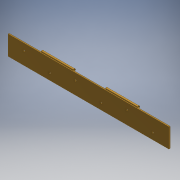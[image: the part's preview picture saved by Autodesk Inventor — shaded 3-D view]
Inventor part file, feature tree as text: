
AUTODESK INVENTOR PART (.ipt)
format: ipt  version: 2018 (Build 220112000, 112)  size: 174,080 bytes
history: native  units: mm
features: extrude x5, sketch x5, hole x1
ambient origin geometry x8: Origin, YZ Plane, XZ Plane, XY Plane, X Axis, Y Axis, Z Axis, Center Point
bodies: Solid1 (feature_tree)
feature tree (11):
  extrude  "Extrusion1"  Depth=30.0mm
  sketch  "Sketch2"  dims[d2=2.0mm d3=0.0mm d4=2.5mm]
  extrude  "Extrusion2"  Depth=2.0mm
  extrude  "Extrusion3"  Depth=3.5mm
  extrude  "Extrusion4"  Depth=250.0mm TaperAngle=0.0deg
  extrude  "Extrusion5"  Depth=2.0mm
  hole  "Hole1"  [1 undecoded]
  sketch  "Sketch1"  dims[d0=250.0mm d1=30.0mm]
  sketch  "Sketch3"  dims[d5=3.0mm d6=3.5mm]
  sketch  "Sketch4"  dims[d7=250.0mm d8=0.0mm d9=250.0mm d10=0.0mm]
  sketch  "Sketch5"  dims[d11=50.0mm d12=2.75mm d13=50.0mm d14=2.75mm d15=50.0mm d16=50.0mm d17=2.75mm d18=50.0mm d19=250.0mm d20=0.0mm d21=250.0mm d22=0.0mm d23=40.0mm d24=5.0mm d25=40.0mm d26=40.0mm d27=40.0mm d28=40.0mm d29=10.0mm d30=10.0mm d31=3.0mm d32=6.0mm d33=5.0mm d34=2.0mm d35=90.0deg d36=8.0mm d37=20.594885mm]
note: 1 required parameter value undecoded (feature->parameter linkage not recoverable at this tier; creation-order binding heuristic only, values carry confidence <= 0.55)
